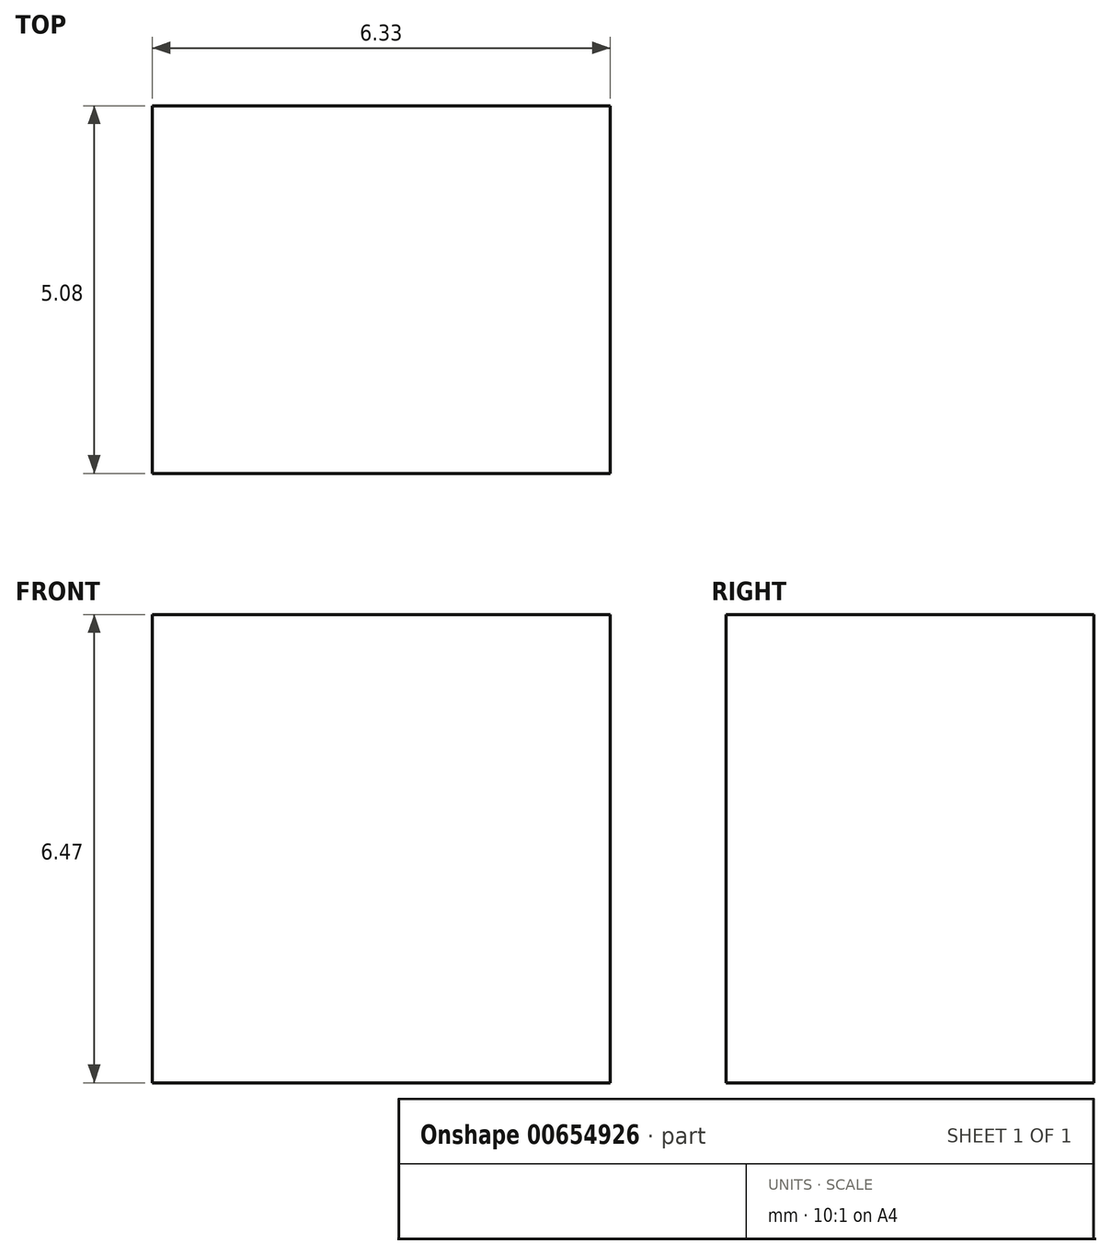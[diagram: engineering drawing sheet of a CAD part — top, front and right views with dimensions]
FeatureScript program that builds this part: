
annotation { "Feature Type Name" : "Feature", "Feature Type Description" : "" }
export const myFeature = defineFeature(function(context is Context, id is Id, definition is map)
    precondition{}
    {
        {
            var Q0;
            Q0=qCreatedBy(makeId("Front.planeOp"),FACE);
            var sketch = newSketch(context, id + "F0", { "sketchPlane" : qUnion([Q0])});
            skLineSegment(sketch, "E0", {"start": v(0, 0) * mm, "end": v(6.33, 0) * mm});
            skLineSegment(sketch, "E1", {"start": v(6.33, 0) * mm, "end": v(6.33, 6.47) * mm});
            skLineSegment(sketch, "E2", {"start": v(6.33, 6.47) * mm, "end": v(0, 6.47) * mm});
            skLineSegment(sketch, "E3", {"start": v(0, 6.47) * mm, "end": v(0, 0) * mm});
            skSolve(sketch);
        }
        {
            var Q0;
            Q0=makeQuery(id+"F0.imprint","IMPRINT",FACE,{"disambiguationData":[TD([[makeQuery(id+"F0.imprint","IMPRINT",EDGE,{"derivedFrom":sQuery(id+"F0.wireOp",EDGE,"E0")}),1.0]])]});
            extrude(context, id + "F1", {"entities" : qUnion([Q0]), "depth" : 5.08 * mm, "offsetDistance" : 25.4 * mm});
        }
    });
